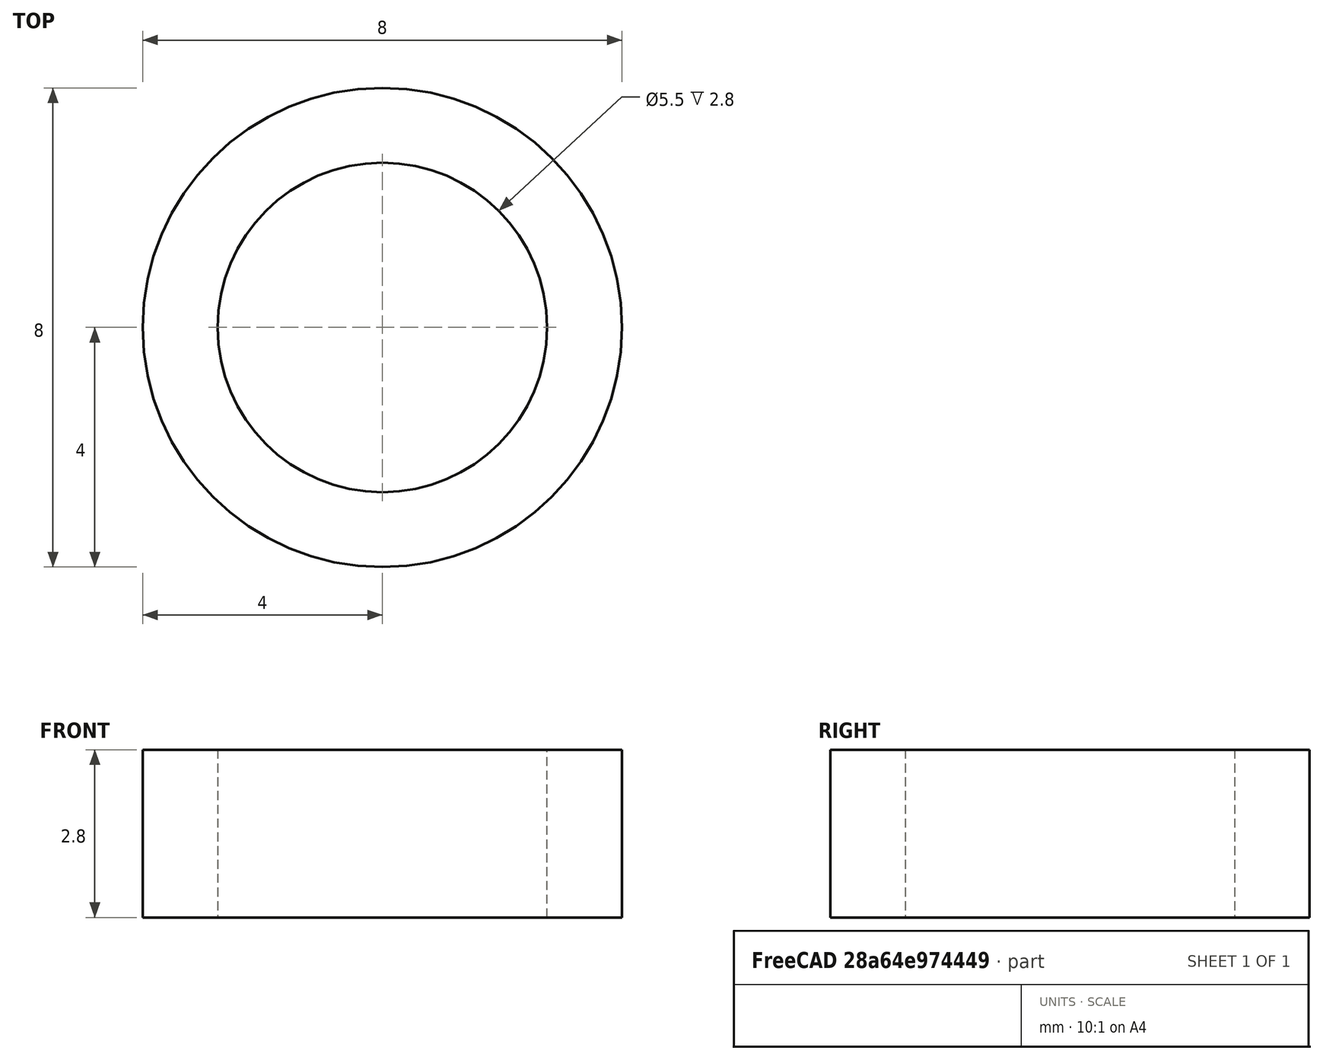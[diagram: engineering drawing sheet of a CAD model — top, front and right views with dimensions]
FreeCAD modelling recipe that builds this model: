
FCSTD DOCUMENT  (FreeCAD 0.20R29603 (Git))
Label: ble finder handle washers
License: All rights reserved
LicenseURL: http://en.wikipedia.org/wiki/All_rights_reserved
objects: Sketcher::SketchObject×1, PartDesign::Pad×1, PartDesign::Body×1
note: 4 computed .brp shape members not serialized (recipe doc carries the construction recipe); baked Part::Feature solids carry a one-line shape summary decoded from their .brp

FEATURE [Sketcher::SketchObject] Sketch
  FullyConstrained = true
  MapMode = 5
  Support = -> [XY_Plane]
  sketch-geometry (2):
    g0: Circle CenterX=0 CenterY=0 CenterZ=0 NormalX=0 NormalY=0 NormalZ=1 AngleXU=0 Radius=2.75
    g1: Circle CenterX=0 CenterY=0 CenterZ=0 NormalX=0 NormalY=0 NormalZ=1 AngleXU=0 Radius=4
  constraints (4):
    c: Coincident(g0,g-1)
    c: Coincident(g1,g0)
    c: Diameter(g0) = 5.5
    c: Diameter(g1) = 8
FEATURE [PartDesign::Pad] Pad
  Direction = (0,0,1)
  Length = 2.8
  Length2 = 10
  Profile = -> Sketch
  ReferenceAxis = -> Sketch [N_Axis]
  Type = 0
FEATURE [PartDesign::Body] Body
  Group = -> [Sketch,Pad]
  Origin = -> Origin
  Tip = -> Pad
